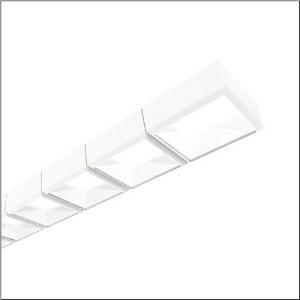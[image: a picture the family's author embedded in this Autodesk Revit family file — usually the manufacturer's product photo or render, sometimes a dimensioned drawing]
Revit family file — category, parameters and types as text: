
# Revit family: scriptus_r__11_5mz212d03wa_20e5
name_source: partatom
category: Lighting Fixtures
units: mm (PartAtom-declared; Revit-internal decimal feet)

## family parameters
Cut with Voids When Loaded = No
Host = Face
Light Source = No
Part Type = Normal
Room Calculation Point = No
Round Connector Dimension = Use Diameter
Shared = No

## types (1)
- Scriptus® 11 (1 x LED 3000K / CRI = 80 (unbekannt), 2200 lm, 3000K)
    Apparent Load = 35 VA
    CIE Flux Codes = 82 95 99 100 100
    Color Rendering = 80
    Color Temperature = 3000K
    Default Elevation = 1800 mm
    Description = Scriptus® 11, office luminaire, primary optical cover: lenses, CAT 2 (L<= 3000cd/m²), light emission: direct distribution, primary light characteristic: symmetric, installation type: surface-mounted, LED, rated luminous flux: 4.390lm, luminous efficacy: 127lm/W, light colour: 830, colour temperature: 3000K, control gear: DALI, with terminal, 5-pole, mains connection: 230V, AC, 50Hz, rated input power: 35W, housing, luminaire housing, of aluminium, traffic white (RAL 9016), length: 1.658mm, width: 114mm, height: 57mm, protection rating (complete): IP20, insulation class (complete): insulation class I (protective earthing), certification: CE, ENEC, VDE, protection symbol: F, permissible operating ambient temperature: 0..+35°C, standard: EN 50419, packaging unit: 1 piece
    Height = 57 mm
    Lamp = 1 x LED 3000K / CRI >= 80 (unbekannt)
    Lamp Light Flux = 2200 lm
    Lamp count = 1
    Length = 1658 mm
    Luminous efficacy = 127 lm/W
    Manufacturer = Siteco
    ModVariant = No
    Model = 5MZ212D03WA
    Mounting Place = Ceiling
    Mounting Type = Surface mounted
    Number of Poles = 1
    OnlyDefault = Yes
    Power Factor = 1
    Product Name = Scriptus® 11
    Product group = office luminaire | ceiling mounted
    ProductGroupID = 302
    Protection Class = Protection class I
    Protection Degree = IP 20
    RLX_Detail_Level = 1
    RLX_Emergency_Light_Flux = 0 lm
    RLX_Emergency_Type = 0
    RLX_Emergency_Type_DB = No
    RlxData = <blob elided: 29465 chars, md5=bac493ae>
    Socket = socket
    Standby Power = 0 W
    System Light Flux = 4400 lm
    System Power = 35 W
    Type Comments = Product without accessories
    Type Image = l_1004833.jpg
    URL = http://relux.com
    VarID = ---
    Voltage = 0 V
    Weight = 0.00 kg
    Width = 114 mm

## geometry (parser evidence)
native form markers: Blend x4, Sweep x14
no freeform markers — native parametric forms only
